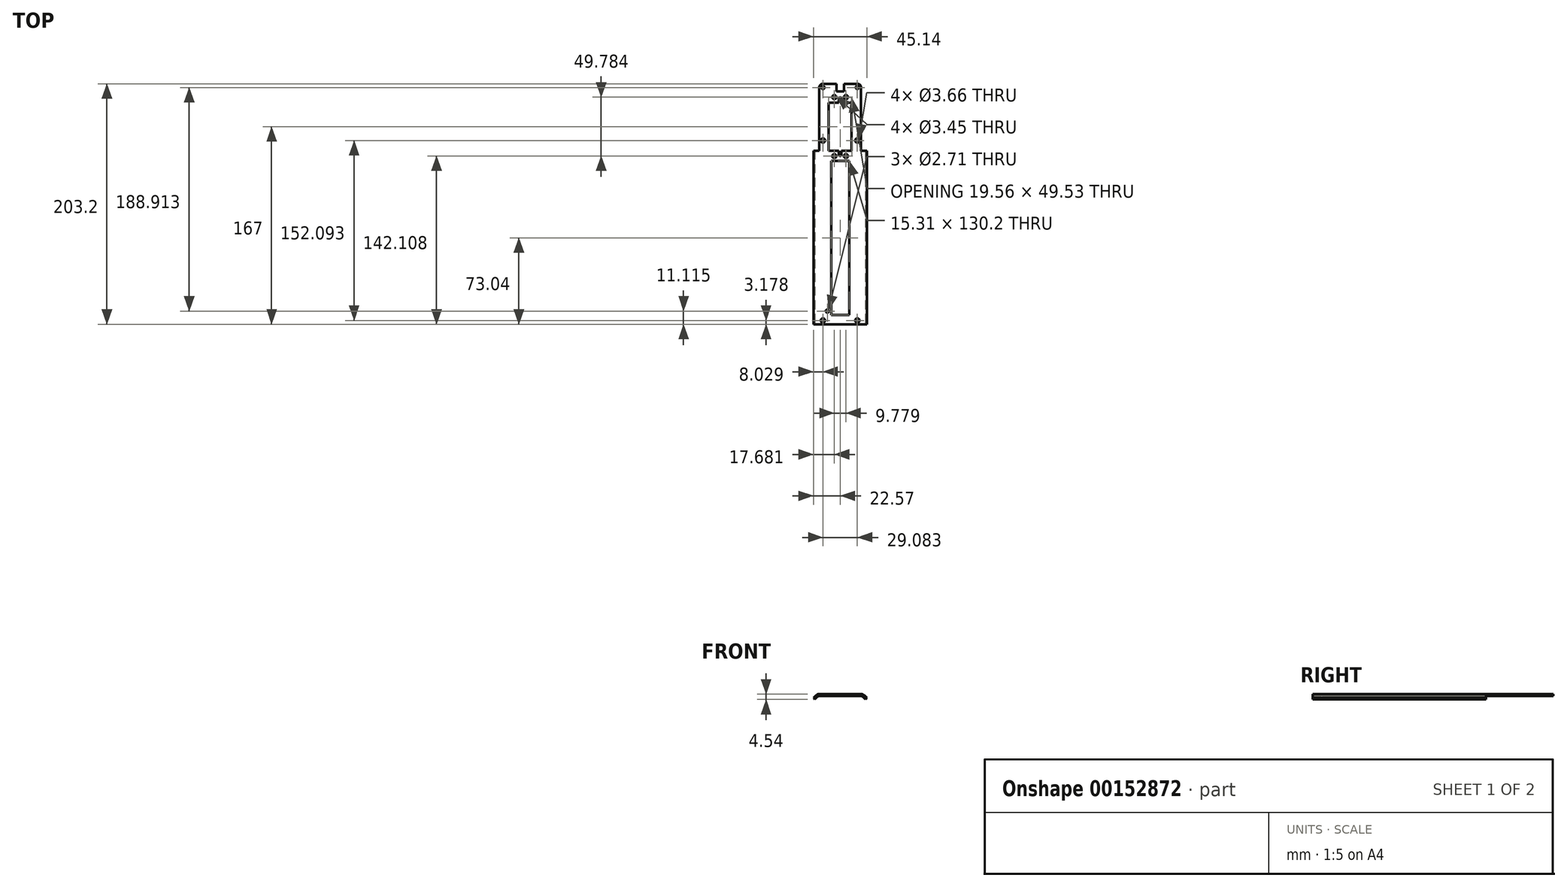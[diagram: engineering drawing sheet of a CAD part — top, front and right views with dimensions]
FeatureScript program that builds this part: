
annotation { "Feature Type Name" : "Feature", "Feature Type Description" : "" }
export const myFeature = defineFeature(function(context is Context, id is Id, definition is map)
    precondition{}
    {
        {
            var Q0;
            Q0=qCreatedBy(makeId("Top.planeOp"),FACE);
            var sketch = newSketch(context, id + "F0", { "sketchPlane" : qUnion([Q0])});
            skLineSegment(sketch, "E0.bottom", {"start": v(9.78, -20.32) * mm, "end": v(-9.78, -20.32) * mm});
            skLineSegment(sketch, "E0.top", {"start": v(9.78, 20.32) * mm, "end": v(-9.78, 20.32) * mm});
            skLineSegment(sketch, "E0.left", {"start": v(9.78, -20.32) * mm, "end": v(9.78, 20.32) * mm});
            skLineSegment(sketch, "E0.right", {"start": v(-9.78, -20.32) * mm, "end": v(-9.78, 20.32) * mm});
            skPoint(sketch, "E0.middle", {"position": v(0, 0) * mm});
            skLineSegment(sketch, "E1.bottom", {"start": v(4.89, 24.9) * mm, "end": v(-4.89, 24.9) * mm, "construction": true});
            skLineSegment(sketch, "E1.top", {"start": v(4.89, -24.9) * mm, "end": v(-4.89, -24.9) * mm, "construction": true});
            skLineSegment(sketch, "E1.left", {"start": v(4.89, 24.9) * mm, "end": v(4.89, -24.9) * mm, "construction": true});
            skLineSegment(sketch, "E1.right", {"start": v(-4.89, 24.9) * mm, "end": v(-4.89, -24.9) * mm, "construction": true});
            skCircle(sketch, "E2", {"center": v(-4.89, 24.9) * mm, "radius": 1.73 * mm});
            skCircle(sketch, "E3", {"center": v(-4.89, -24.9) * mm, "radius": 1.73 * mm});
            skCircle(sketch, "E4", {"center": v(4.89, -24.9) * mm, "radius": 1.73 * mm});
            skCircle(sketch, "E5", {"center": v(4.89, 24.9) * mm, "radius": 1.73 * mm});
            skLineSegment(sketch, "E6", {"start": v(-17.72, 36.2) * mm, "end": v(17.72, 36.2) * mm});
            skLineSegment(sketch, "E7", {"start": v(-17.72, 36.2) * mm, "end": v(-17.72, -167) * mm});
            skLineSegment(sketch, "E8", {"start": v(-17.72, -167) * mm, "end": v(17.72, -167) * mm});
            skLineSegment(sketch, "E9", {"start": v(17.72, -167) * mm, "end": v(17.72, 36.2) * mm});
            skLineSegment(sketch, "E10", {"start": v(0, -167) * mm, "end": v(0, -163.82) * mm, "construction": true});
            skLineSegment(sketch, "E11", {"start": v(14.54, -163.82) * mm, "end": v(-14.54, -163.82) * mm, "construction": true});
            skLineSegment(sketch, "E12", {"start": v(-14.54, -163.82) * mm, "end": v(-17.72, -163.82) * mm, "construction": true});
            skCircle(sketch, "E13", {"center": v(-14.54, -163.82) * mm, "radius": 1.83 * mm});
            skCircle(sketch, "E14", {"center": v(14.54, -163.82) * mm, "radius": 1.83 * mm});
            skLineSegment(sketch, "E15", {"start": v(14.54, 20.32) * mm, "end": v(14.54, -11.73) * mm, "construction": true});
            skCircle(sketch, "E16", {"center": v(14.54, -11.73) * mm, "radius": 1.83 * mm});
            skLineSegment(sketch, "E17", {"start": v(0, 24.9) * mm, "end": v(0, 33.03) * mm, "construction": true});
            skLineSegment(sketch, "E18", {"start": v(-14.54, 33.03) * mm, "end": v(14.54, 33.03) * mm, "construction": true});
            skCircle(sketch, "E19", {"center": v(-14.54, 33.03) * mm, "radius": 1.35 * mm});
            skCircle(sketch, "E20", {"center": v(14.54, 33.03) * mm, "radius": 1.35 * mm});
            skLineSegment(sketch, "E21", {"start": v(0, 33.03) * mm, "end": v(0, 36.2) * mm, "construction": true});
            skLineSegment(sketch, "E22", {"start": v(14.54, 33.03) * mm, "end": v(17.72, 33.03) * mm, "construction": true});
            skLineSegment(sketch, "E23", {"start": v(9.78, 20.32) * mm, "end": v(14.54, 20.32) * mm, "construction": true});
            skLineSegment(sketch, "E24", {"start": v(-9.78, 20.32) * mm, "end": v(-14.54, 20.32) * mm, "construction": true});
            skLineSegment(sketch, "E25", {"start": v(-14.54, 20.32) * mm, "end": v(-14.54, -11.73) * mm, "construction": true});
            skCircle(sketch, "E26", {"center": v(-14.54, -11.73) * mm, "radius": 1.83 * mm});
            skLineSegment(sketch, "E27", {"start": v(14.54, 4.3) * mm, "end": v(17.72, 4.3) * mm, "construction": true});
            skLineSegment(sketch, "E28", {"start": v(0, 20.32) * mm, "end": v(0, 10.9) * mm, "construction": true});
            skLineSegment(sketch, "E29.bottom", {"start": v(-7.65, -28.86) * mm, "end": v(7.65, -28.86) * mm});
            skLineSegment(sketch, "E29.top", {"start": v(-7.65, -159.06) * mm, "end": v(7.65, -159.06) * mm});
            skLineSegment(sketch, "E29.left", {"start": v(-7.65, -28.86) * mm, "end": v(-7.65, -159.06) * mm});
            skLineSegment(sketch, "E29.right", {"start": v(7.65, -28.86) * mm, "end": v(7.65, -159.06) * mm});
            skLineSegment(sketch, "E30", {"start": v(0, -163.82) * mm, "end": v(0, -159.06) * mm, "construction": true});
            skLineSegment(sketch, "E31", {"start": v(0, -24.9) * mm, "end": v(0, -28.86) * mm, "construction": true});
            skLineSegment(sketch, "E32", {"start": v(-7.65, -159.06) * mm, "end": v(-10.83, -159.06) * mm, "construction": true});
            skLineSegment(sketch, "E33", {"start": v(-10.83, -159.06) * mm, "end": v(-10.83, -155.88) * mm, "construction": true});
            skCircle(sketch, "E34", {"center": v(-10.83, -155.88) * mm, "radius": 1.35 * mm});
            skSolve(sketch);
        }
        {
            var Q0;
            Q0 = qSketchRegion(id + "F0", true);
            extrude(context, id + "F1", {"entities" : qUnion([Q0]), "depth" : 1.7 * mm});
        }
        {
            var Q0;
            Q0=makeQuery(id+"F1.opExtrude","SWEPT_FACE",FACE,{"disambiguationData":[OSD([sQuery(id+"F0.wireOp",EDGE,"E8")])]});
            var sketch = newSketch(context, id + "F2", { "sketchPlane" : qUnion([Q0])});
            skArc(sketch, "E35", {"start": v(-17.72, 0) * mm, "mid": v(-18.48, -0.15) * mm, "end": v(-19.12, -0.58) * mm});
            skArc(sketch, "E36", {"start": v(-17.72, 1.7) * mm, "mid": v(-19.13, 1.43) * mm, "end": v(-20.33, 0.63) * mm});
            skArc(sketch, "E37", {"start": v(19.12, -0.58) * mm, "mid": v(18.48, -0.15) * mm, "end": v(17.72, 0) * mm});
            skArc(sketch, "E38", {"start": v(20.33, 0.63) * mm, "mid": v(19.13, 1.43) * mm, "end": v(17.72, 1.7) * mm});
            skLineSegment(sketch, "E39.bottom", {"start": v(-20.33, 0.63) * mm, "end": v(-22.57, -1.62) * mm});
            skLineSegment(sketch, "E39.top", {"start": v(-19.12, -0.58) * mm, "end": v(-21.36, -2.83) * mm});
            skLineSegment(sketch, "E39.left", {"start": v(-20.33, 0.63) * mm, "end": v(-19.12, -0.58) * mm, "construction": true});
            skLineSegment(sketch, "E39.right", {"start": v(-22.57, -1.62) * mm, "end": v(-21.36, -2.83) * mm});
            skLineSegment(sketch, "E40", {"start": v(-17.72, 1.7) * mm, "end": v(-17.72, 0) * mm});
            skLineSegment(sketch, "E41.bottom", {"start": v(20.33, 0.63) * mm, "end": v(22.57, -1.62) * mm});
            skLineSegment(sketch, "E41.top", {"start": v(19.12, -0.58) * mm, "end": v(21.36, -2.83) * mm});
            skLineSegment(sketch, "E41.left", {"start": v(20.33, 0.63) * mm, "end": v(19.12, -0.58) * mm, "construction": true});
            skLineSegment(sketch, "E41.right", {"start": v(22.57, -1.62) * mm, "end": v(21.36, -2.83) * mm});
            skLineSegment(sketch, "E42", {"start": v(19.12, -0.58) * mm, "end": v(-19.12, -0.58) * mm, "construction": true});
            skLineSegment(sketch, "E43", {"start": v(0, 0) * mm, "end": v(0, -0.58) * mm, "construction": true});
            skSolve(sketch);
        }
        {
            var Q0;
            Q0 = qSketchRegion(id + "F2", true);
            var Q1;
            Q1=makeQuery(id+"F2.imprint","IMPRINT",FACE,{"disambiguationData":[TD([[makeQuery(id+"F2.imprint","IMPRINT",EDGE,{"derivedFrom":sQuery(id+"F2.wireOp",EDGE,"E37")}),-1.0]])]});
            var Q2;
            Q2=makeQuery(id+"F1.opExtrude","SWEPT_FACE",FACE,{"disambiguationData":[OSD([sQuery(id+"F0.wireOp",EDGE,"E0.bottom")])]});
            extrude(context, id + "F3", {"entities" : qUnion([Q0, Q1]), "operationType" : NewBodyOperationType.ADD, "endBound" : BoundingType.UP_TO_SURFACE, "oppositeDirection" : true, "endBoundEntityFace" : qUnion([Q2]), "depth" : 25.4 * mm});
        }
        {
            var Q0;
            Q0=makeQuery(id+"F1.opExtrude","SWEPT_EDGE",EDGE,{"disambiguationData":[OSD([sQuery(id+"F0.wireOp",EDGE,"E6"),sQuery(id+"F0.wireOp",EDGE,"E9")])]});
            var Q1;
            Q1=makeQuery(id+"F1.opExtrude","SWEPT_EDGE",EDGE,{"disambiguationData":[OSD([sQuery(id+"F0.wireOp",EDGE,"E6"),sQuery(id+"F0.wireOp",EDGE,"E7")])]});
            fillet(context, id + "F4", {"entities" : qUnion([Q0, Q1]), "radius" : 3.17 * mm, "allowEdgeOverflow" : false});
        }
        {
            var Q0;
            Q0=makeQuery(id+"F1.opExtrude","CAP_FACE",FACE,{"disambiguationData":[OSD([sQuery(id+"F0.wireOp",EDGE,"E0.bottom"),sQuery(id+"F0.wireOp",EDGE,"E0.top"),sQuery(id+"F0.wireOp",EDGE,"E0.left"),sQuery(id+"F0.wireOp",EDGE,"E0.right"),sQuery(id+"F0.wireOp",EDGE,"E2"),sQuery(id+"F0.wireOp",EDGE,"E3"),sQuery(id+"F0.wireOp",EDGE,"E4"),sQuery(id+"F0.wireOp",EDGE,"E5"),sQuery(id+"F0.wireOp",EDGE,"E6"),sQuery(id+"F0.wireOp",EDGE,"E7"),sQuery(id+"F0.wireOp",EDGE,"E8"),sQuery(id+"F0.wireOp",EDGE,"E9"),sQuery(id+"F0.wireOp",EDGE,"E13"),sQuery(id+"F0.wireOp",EDGE,"E14"),sQuery(id+"F0.wireOp",EDGE,"NSqTDclR-uUfq-642O-bPFq-7ZzSKmZckV6j"),sQuery(id+"F0.wireOp",EDGE,"E16"),sQuery(id+"F0.wireOp",EDGE,"E19"),sQuery(id+"F0.wireOp",EDGE,"E20"),sQuery(id+"F0.wireOp",EDGE,"kX7Uj1Lz-vubc-PjqN-hmpr-YgtDeQjNjYQ9"),sQuery(id+"F0.wireOp",EDGE,"E26")])],"isStart":false});
            var sketch = newSketch(context, id + "F5", { "sketchPlane" : qUnion([Q0])});
            skLineSegment(sketch, "E44.bottom", {"start": v(-3.17, 36.2) * mm, "end": v(3.17, 36.2) * mm});
            skLineSegment(sketch, "E44.top", {"start": v(-3.18, 29.85) * mm, "end": v(3.18, 29.85) * mm});
            skLineSegment(sketch, "E44.left", {"start": v(-3.18, 36.2) * mm, "end": v(-3.18, 29.85) * mm});
            skLineSegment(sketch, "E44.right", {"start": v(3.17, 36.2) * mm, "end": v(3.17, 29.85) * mm});
            skPoint(sketch, "E45", {"position": v(0, 36.2) * mm});
            skPoint(sketch, "E46", {"position": v(0, 20.32) * mm});
            skPoint(sketch, "E47", {"position": v(0, -20.32) * mm});
            skLineSegment(sketch, "E48.bottom", {"start": v(1.02, -20.32) * mm, "end": v(-1.02, -20.32) * mm});
            skLineSegment(sketch, "E48.top", {"start": v(1.02, -23.75) * mm, "end": v(-1.02, -23.75) * mm, "construction": true});
            skLineSegment(sketch, "E48.left", {"start": v(1.02, -20.32) * mm, "end": v(1.02, -23.75) * mm});
            skLineSegment(sketch, "E48.right", {"start": v(-1.02, -20.32) * mm, "end": v(-1.02, -23.75) * mm});
            skLineSegment(sketch, "E49.bottom", {"start": v(1.02, 20.32) * mm, "end": v(-1.02, 20.32) * mm});
            skLineSegment(sketch, "E49.top", {"start": v(1.02, 23.75) * mm, "end": v(-1.02, 23.75) * mm, "construction": true});
            skLineSegment(sketch, "E49.left", {"start": v(1.02, 20.32) * mm, "end": v(1.02, 23.75) * mm});
            skLineSegment(sketch, "E49.right", {"start": v(-1.02, 20.32) * mm, "end": v(-1.02, 23.75) * mm});
            skArc(sketch, "E50", {"start": v(1.02, 23.75) * mm, "mid": v(0, 24.77) * mm, "end": v(-1.02, 23.75) * mm});
            skArc(sketch, "E51", {"start": v(-1.02, -23.75) * mm, "mid": v(0, -24.77) * mm, "end": v(1.02, -23.75) * mm});
            skSolve(sketch);
        }
        {
            var Q0;
            Q0 = qSketchRegion(id + "F5", true);
            var Q1;
            Q1=makeQuery(id+"F1.opExtrude","CAP_FACE",FACE,{"disambiguationData":[OSD([sQuery(id+"F0.wireOp",EDGE,"E0.bottom"),sQuery(id+"F0.wireOp",EDGE,"E0.top"),sQuery(id+"F0.wireOp",EDGE,"E0.left"),sQuery(id+"F0.wireOp",EDGE,"E0.right"),sQuery(id+"F0.wireOp",EDGE,"E2"),sQuery(id+"F0.wireOp",EDGE,"E3"),sQuery(id+"F0.wireOp",EDGE,"E4"),sQuery(id+"F0.wireOp",EDGE,"E5"),sQuery(id+"F0.wireOp",EDGE,"E6"),sQuery(id+"F0.wireOp",EDGE,"E7"),sQuery(id+"F0.wireOp",EDGE,"E8"),sQuery(id+"F0.wireOp",EDGE,"E9"),sQuery(id+"F0.wireOp",EDGE,"E13"),sQuery(id+"F0.wireOp",EDGE,"E14"),sQuery(id+"F0.wireOp",EDGE,"NSqTDclR-uUfq-642O-bPFq-7ZzSKmZckV6j"),sQuery(id+"F0.wireOp",EDGE,"E16"),sQuery(id+"F0.wireOp",EDGE,"E19"),sQuery(id+"F0.wireOp",EDGE,"E20"),sQuery(id+"F0.wireOp",EDGE,"kX7Uj1Lz-vubc-PjqN-hmpr-YgtDeQjNjYQ9"),sQuery(id+"F0.wireOp",EDGE,"E26")])],"isStart":true});
            extrude(context, id + "F6", {"entities" : qUnion([Q0]), "operationType" : NewBodyOperationType.REMOVE, "endBound" : BoundingType.UP_TO_SURFACE, "oppositeDirection" : true, "endBoundEntityFace" : qUnion([Q1]), "depth" : 25.4 * mm});
        }
    });
